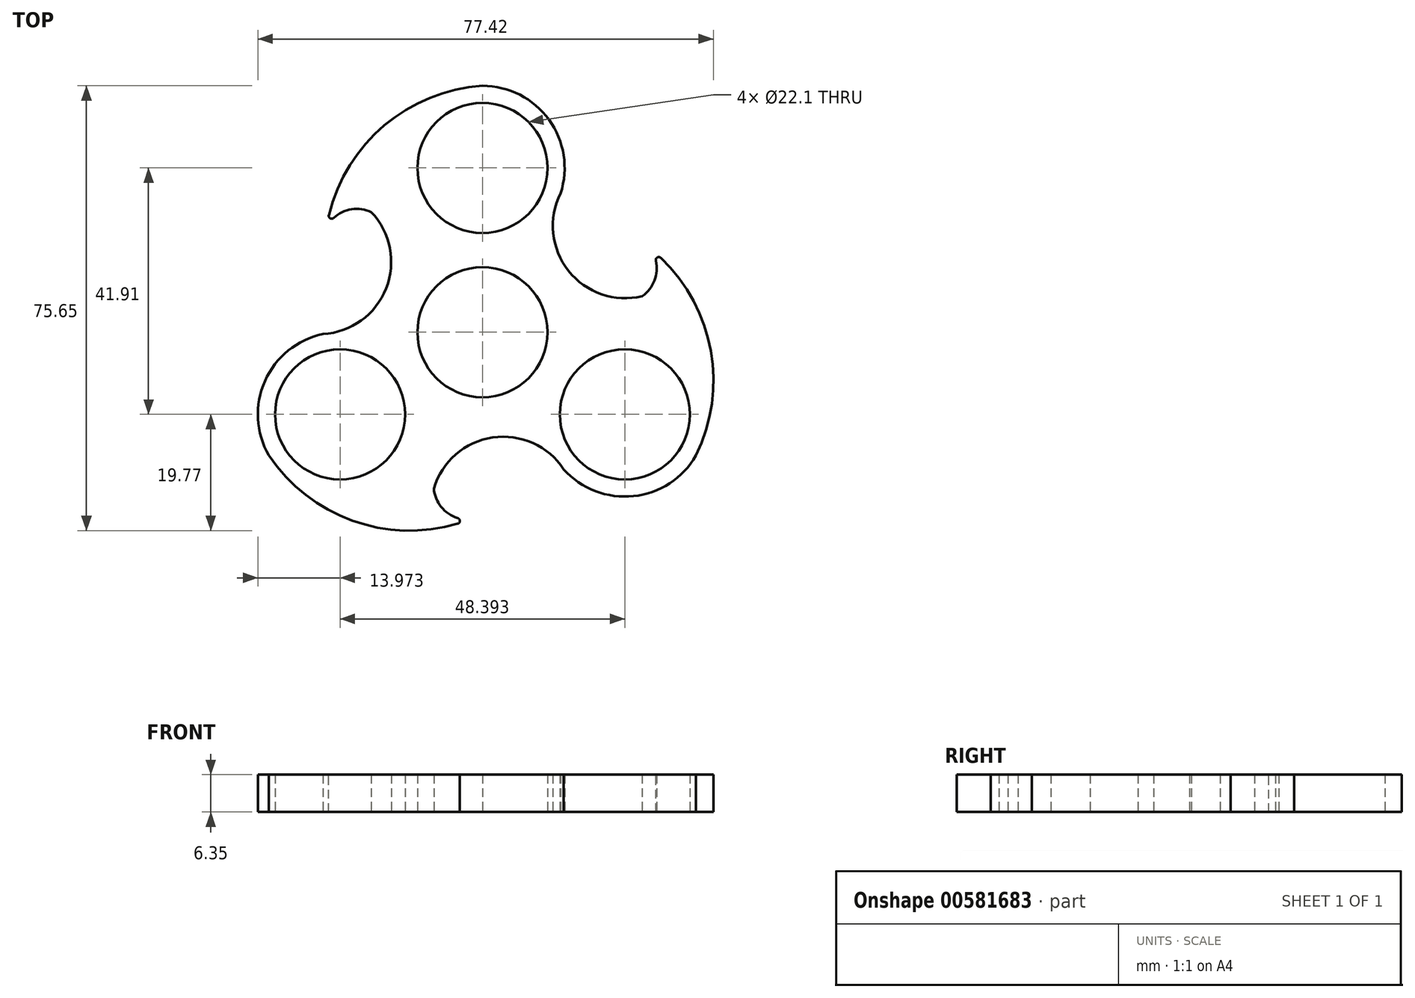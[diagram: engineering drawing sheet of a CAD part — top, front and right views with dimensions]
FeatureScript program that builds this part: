
annotation { "Feature Type Name" : "Feature", "Feature Type Description" : "" }
export const myFeature = defineFeature(function(context is Context, id is Id, definition is map)
    precondition{}
    {
        {
            var Q0;
            Q0=qCreatedBy(makeId("Top.planeOp"),FACE);
            var sketch = newSketch(context, id + "F0", { "sketchPlane" : qUnion([Q0])});
            skCircle(sketch, "E0", {"center": v(0, 0) * mm, "radius": 11.05 * mm});
            skCircle(sketch, "E1", {"center": v(0, 27.94) * mm, "radius": 11.05 * mm});
            skCircle(sketch, "E2.1.0", {"center": v(-24.2, -13.97) * mm, "radius": 11.05 * mm});
            skCircle(sketch, "E2.2.0", {"center": v(24.2, -13.97) * mm, "radius": 11.05 * mm});
            skArc(sketch, "E3", {"start": v(12.54, 21.78) * mm, "mid": v(10.8, 36.8) * mm, "end": v(-3.59, 41.44) * mm});
            skArc(sketch, "E4", {"start": v(-25.13, -0.03) * mm, "mid": v(-37.27, -9.05) * mm, "end": v(-34.1, -23.83) * mm});
            skArc(sketch, "E5", {"start": v(12.6, -21.75) * mm, "mid": v(26.47, -27.75) * mm, "end": v(37.68, -17.61) * mm});
            skPoint(sketch, "E6.start.orphan", {"position": v(0, 41.91) * mm});
            skArc(sketch, "E7", {"start": v(-18.88, 20.44) * mm, "mid": v(-23.33, 20.64) * mm, "end": v(-26.57, 17.6) * mm});
            skPoint(sketch, "E8.startSnap0", {"position": v(-15.2, 14.45) * mm});
            skArc(sketch, "E9", {"start": v(0, 41.91) * mm, "mid": v(-17.55, 34.4) * mm, "end": v(-26.57, 17.6) * mm});
            skArc(sketch, "E10.1.0", {"start": v(-36.3, -20.95) * mm, "mid": v(-21.03, -32.4) * mm, "end": v(-1.95, -31.81) * mm});
            skArc(sketch, "E10.1.1", {"start": v(-8.26, -26.57) * mm, "mid": v(-6.21, -30.52) * mm, "end": v(-1.95, -31.81) * mm});
            skArc(sketch, "E10.2.0", {"start": v(36.3, -20.96) * mm, "mid": v(38.57, -2) * mm, "end": v(28.53, 14.22) * mm});
            skArc(sketch, "E10.2.1", {"start": v(27.14, 6.14) * mm, "mid": v(29.54, 9.88) * mm, "end": v(28.53, 14.22) * mm});
            skArc(sketch, "E11", {"start": v(13.81, -23.32) * mm, "mid": v(1.74, -17.9) * mm, "end": v(-8.26, -26.57) * mm});
            skArc(sketch, "E12.1.0", {"start": v(13.29, 23.62) * mm, "mid": v(14.63, 10.46) * mm, "end": v(27.14, 6.14) * mm});
            skArc(sketch, "E12.2.0", {"start": v(-27.1, -0.3) * mm, "mid": v(-16.37, 7.44) * mm, "end": v(-18.88, 20.44) * mm});
            skPoint(sketch, "E13.end.orphan", {"position": v(-15.2, 4.25) * mm});
            skSolve(sketch);
        }
        {
            var Q0;
            Q0=makeQuery(id+"F0.imprint","IMPRINT",FACE,{"disambiguationData":[TD([[makeQuery(id+"F0.imprint","IMPRINT",EDGE,{"derivedFrom":sQuery(id+"F0.wireOp",EDGE,"E1")}),-1.0]])]});
            var Q1;
            Q1=makeQuery(id+"F0.imprint","IMPRINT",FACE,{"disambiguationData":[TD([[makeQuery(id+"F0.imprint","IMPRINT",EDGE,{"derivedFrom":sQuery(id+"F0.wireOp",EDGE,"E2.2.0")}),-1.0]])]});
            var Q2;
            Q2=makeQuery(id+"F0.imprint","IMPRINT",FACE,{"disambiguationData":[TD([[makeQuery(id+"F0.imprint","IMPRINT",EDGE,{"derivedFrom":sQuery(id+"F0.wireOp",EDGE,"E2.1.0")}),-1.0]])]});
            var Q3;
            Q3=makeQuery(id+"F0.imprint","IMPRINT",FACE,{"disambiguationData":[TD([[makeQuery(id+"F0.imprint","IMPRINT",EDGE,{"derivedFrom":sQuery(id+"F0.wireOp",EDGE,"4O9khdKf-2qk6-6eEU-YUye-EU3OGTiNBHui")}),-1.0]])]});
            var Q4;
            Q4=makeQuery(id+"F0.imprint","IMPRINT",FACE,{"disambiguationData":[TD([[makeQuery(id+"F0.imprint","IMPRINT",EDGE,{"derivedFrom":sQuery(id+"F0.wireOp",EDGE,"E0")}),-1.0]])]});
            extrude(context, id + "F1", {"entities" : qUnion([Q0, Q1, Q2, Q3, Q4]), "depth" : 6.35 * mm});
        }
        {
            var Q0;
            Q0=makeQuery(id+"F1.opExtrude","SWEPT_EDGE",EDGE,{"disambiguationData":[OSD([sQuery(id+"F0.wireOp",EDGE,"E10.1.0"),sQuery(id+"F0.wireOp",EDGE,"E10.1.1")])]});
            var Q1;
            Q1=makeQuery(id+"F1.opExtrude","SWEPT_EDGE",EDGE,{"disambiguationData":[OSD([sQuery(id+"F0.wireOp",EDGE,"E7"),sQuery(id+"F0.wireOp",EDGE,"E9")])]});
            var Q2;
            Q2=makeQuery(id+"F1.opExtrude","SWEPT_EDGE",EDGE,{"disambiguationData":[OSD([sQuery(id+"F0.wireOp",EDGE,"E10.2.0"),sQuery(id+"F0.wireOp",EDGE,"E10.2.1")])]});
            fillet(context, id + "F2", {"entities" : qUnion([Q0, Q1, Q2]), "radius" : 0.5 * mm, "tangentPropagation" : true, "allowEdgeOverflow" : false});
        }
    });
